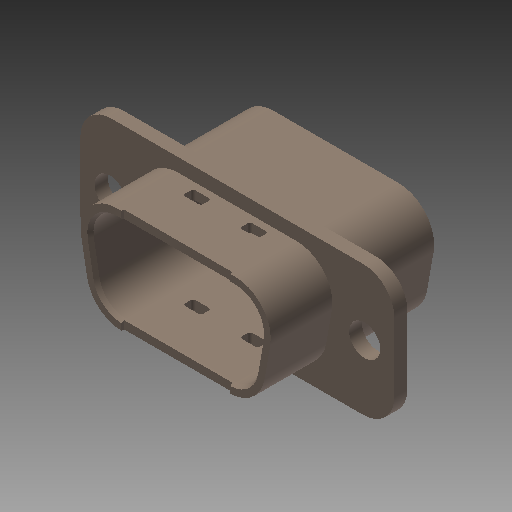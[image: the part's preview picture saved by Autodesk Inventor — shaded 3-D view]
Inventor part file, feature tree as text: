
AUTODESK INVENTOR PART (.ipt)
format: ipt  version: 2017 (Build 210142000, 142)  size: 252,416 bytes
history: native  units: in
note: dims shown in document units (in); Inventor stores cm internally (conversion verified against a paired STEP export)
features: mirror x1
ambient origin geometry x8: Origin, YZ Plane, XZ Plane, XY Plane, X Axis, Y Axis, Z Axis, Center Point
bodies: Solid1 (feature_tree)
feature tree (1):
  mirror  "Mirror1"
